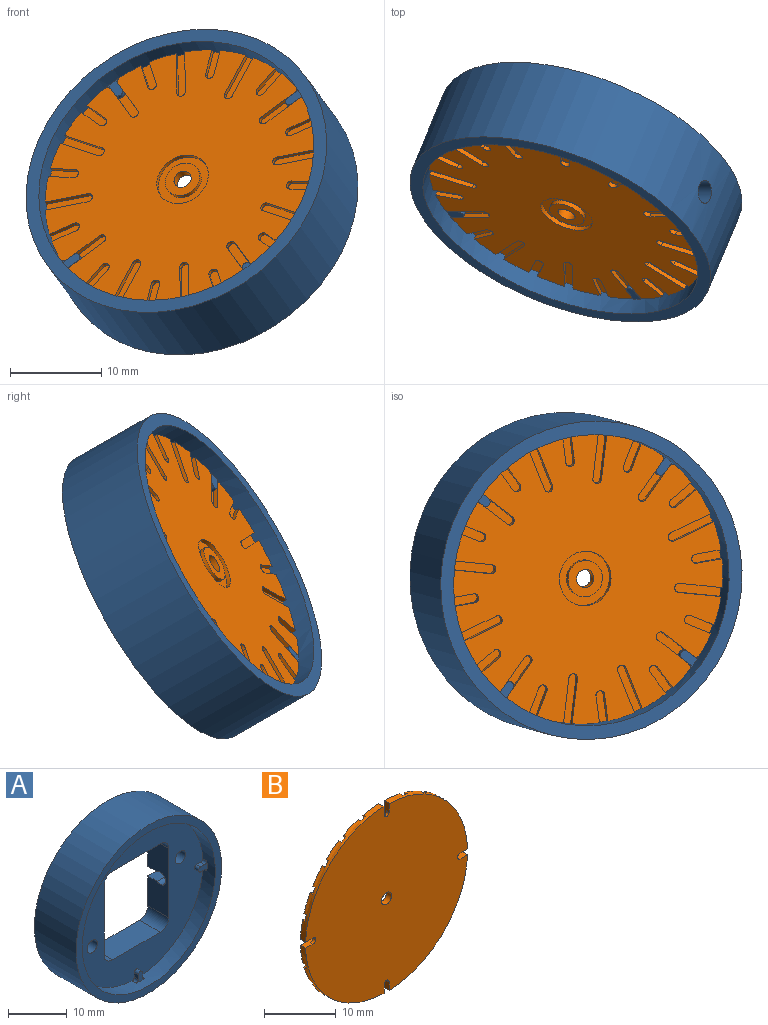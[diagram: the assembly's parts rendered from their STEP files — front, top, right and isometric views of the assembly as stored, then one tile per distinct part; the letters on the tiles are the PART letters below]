
ASSEMBLY  parts=2 mates=1
PART A: 45 faces, bbox 35x10x35 mm
  f0: cylinder r=16mm len=32mm, axis (0,-1,0), area 293.3mm2, adj f1,f7,f21,f25,f29,f33,f37,f38
  f1: plane 31.94x31.94mm, normal (0,-1,0), area 504.1mm2, adj f0,f2,f3,f4,f5,f11,f12,f13
  f2: plane 14.41x5mm, normal (-1,0,0), area 63.3mm2, adj f1,f10,f13,f14,f17,f19,f20
  f3: plane 11.52x5mm, normal (0,0,1), area 57.6mm2, adj f1,f10,f12,f14
  f4: plane 14.41x5mm, normal (1,0,0), area 72mm2, adj f1,f10,f11,f12
  f5: plane 11.52x5mm, normal (0,0,-1), area 57.6mm2, adj f1,f10,f11,f13
  f6: plane 35x35mm, normal (0,1,0), area 346.4mm2, adj f8,f9
  f7: plane 35x35mm, normal (0,-1,0), area 157.9mm2, adj f0,f8
  f8: cylinder r=17.5mm len=35mm, axis (0,-1,0), area 1094.7mm2, adj f6,f7,f17
  f9: cylinder r=14mm len=28mm, axis (0,1,0), area 175.9mm2, adj f6,f10
  f10: plane 28x28mm, normal (0,1,0), area 311.6mm2, adj f2,f3,f4,f5,f9,f11,f12,f13
  f11: cylinder r=2mm len=5mm, axis (0,1,0), area 15.7mm2, adj f1,f4,f5,f10
  f12: cylinder r=2mm len=5mm, axis (0,1,0), area 15.7mm2, adj f1,f3,f4,f10
  f13: cylinder r=2mm len=5mm, axis (0,1,0), area 15.7mm2, adj f1,f2,f5,f10
  f14: cylinder r=2mm len=5mm, axis (0,1,0), area 15.7mm2, adj f1,f2,f3,f10
  f15: cylinder r=1.25mm len=5mm, axis (0,1,0), area 39.3mm2, adj f1,f10
  f16: cylinder r=1.25mm len=5mm, axis (0,1,0), area 39.3mm2, adj f1,f10
  f17: cylinder r=1.25mm len=9.74mm, axis (-1,0,0), area 62.4mm2, adj f2,f8,f18,f19,f20
  f18: cylinder r=1mm len=2.25mm, axis (0,1,0), area 6.2mm2, adj f10,f17,f19,f20
  f19: plane 5.24x2.25mm, normal (0,0,-1), area 11.8mm2, adj f2,f10,f17,f18
  f20: plane 5.24x2.25mm, normal (0,0,1), area 11.8mm2, adj f2,f10,f17,f18
  f21: plane 2.06x2mm, normal (0,-1,0), area 2mm2, adj f0,f22,f23,f24,f43,f44
  f22: plane 1x0.97mm, normal (-1,0,0), area 1mm2, adj f1,f21,f24,f43
  f23: plane 1x0.97mm, normal (1,0,0), area 1mm2, adj f1,f21,f24,f44
  f24: cylinder r=0.5mm len=1mm, axis (0,1,0), area 1.6mm2, adj f1,f21,f22,f23
  f25: plane 2.06x2mm, normal (0,-1,0), area 2mm2, adj f0,f26,f27,f28,f39,f40
  f26: plane 1x0.97mm, normal (0,0,1), area 1mm2, adj f1,f25,f28,f39
  f27: plane 1x0.97mm, normal (0,0,-1), area 1mm2, adj f1,f25,f28,f40
  f28: cylinder r=0.5mm len=1mm, axis (0,1,0), area 1.6mm2, adj f1,f25,f26,f27
  f29: plane 2.06x2mm, normal (0,-1,0), area 2mm2, adj f0,f30,f31,f32,f37,f38
  f30: plane 1x0.97mm, normal (1,0,0), area 1mm2, adj f1,f29,f32,f37
  f31: plane 1x0.97mm, normal (-1,0,0), area 1mm2, adj f1,f29,f32,f38
  f32: cylinder r=0.5mm len=1mm, axis (0,1,0), area 1.6mm2, adj f1,f29,f30,f31
  f33: plane 2.06x2mm, normal (0,-1,0), area 2mm2, adj f0,f34,f35,f36,f41,f42
  f34: plane 1x0.97mm, normal (0,0,-1), area 1mm2, adj f1,f33,f36,f41
  f35: plane 1x0.97mm, normal (0,0,1), area 1mm2, adj f1,f33,f36,f42
  f36: cylinder r=0.5mm len=1mm, axis (0,1,0), area 1.6mm2, adj f1,f33,f34,f35
  f37: cylinder r=0.5mm len=1mm, axis (0,-1,0), area 0.8mm2, adj f0,f1,f29,f30
  f38: cylinder r=0.5mm len=1mm, axis (0,-1,0), area 0.8mm2, adj f0,f1,f29,f31
  f39: cylinder r=0.5mm len=1mm, axis (0,-1,0), area 0.8mm2, adj f0,f1,f25,f26
  f40: cylinder r=0.5mm len=1mm, axis (0,-1,0), area 0.8mm2, adj f0,f1,f25,f27
  f41: cylinder r=0.5mm len=1mm, axis (0,-1,0), area 0.8mm2, adj f0,f1,f33,f34
  f42: cylinder r=0.5mm len=1mm, axis (0,-1,0), area 0.8mm2, adj f0,f1,f33,f35
  f43: cylinder r=0.5mm len=1mm, axis (0,-1,0), area 0.8mm2, adj f0,f1,f21,f22
  f44: cylinder r=0.5mm len=1mm, axis (0,-1,0), area 0.8mm2, adj f0,f1,f21,f23
PART B: 115 faces, bbox 32x1x32 mm
  f0: plane 4x4mm, normal (0,1,0), area 9.4mm2, adj f103,f114
  f1: cylinder r=16mm len=15.49mm, axis (0,-1,0), area 21.6mm2, adj f5,f6,f10,f11,f12,f13,f15,f16
  f2: cylinder r=16mm len=15.49mm, axis (0,-1,0), area 21.6mm2, adj f5,f6,f8,f61,f63,f64,f66,f67
  f3: cylinder r=16mm len=15.49mm, axis (0,-1,0), area 21.6mm2, adj f5,f6,f37,f60,f71,f72,f73,f75
  f4: cylinder r=16mm len=15.49mm, axis (0,-1,0), area 21.6mm2, adj f5,f6,f30,f36,f39,f40,f41,f43
  f5: plane 31.98x31.98mm, normal (0,1,0), area 670.6mm2, adj f1,f2,f3,f4,f8,f9,f10,f12
  f6: plane 31.98x31.98mm, normal (0,-1,0), area 793.5mm2, adj f1,f2,f3,f4,f8,f10,f28,f30
  f7: plane 4x1mm, normal (0,1,0), area 3.5mm2, adj f8,f9,f10,f106,f107
  f8: plane 4.99x1mm, normal (-1,0,0), area 3.2mm2, adj f2,f5,f6,f7,f9,f106
  f9: cylinder r=0.5mm len=1mm, axis (0,1,0), area 0.8mm2, adj f5,f7,f8,f10
  f10: plane 4.99x1mm, normal (1,0,0), area 3.2mm2, adj f1,f5,f6,f7,f9,f107
  f11: plane 2.97x2.97mm, normal (0,1,0), area 3.4mm2, adj f1,f12,f13,f14
  f12: plane 2.12x2.12mm, normal (0.71,0,-0.71), area 1.5mm2, adj f1,f5,f11,f14
  f13: plane 2.12x2.12mm, normal (-0.71,0,0.71), area 1.5mm2, adj f1,f5,f11,f14
  f14: cylinder r=0.5mm len=0.85mm, axis (0,1,0), area 0.8mm2, adj f5,f11,f12,f13
  f15: plane 5.07x3.43mm, normal (0,1,0), area 5.4mm2, adj f1,f16,f17,f18
  f16: plane 4.32x2.5mm, normal (-0.5,0,0.87), area 2.5mm2, adj f1,f5,f15,f17
  f17: cylinder r=0.5mm len=0.93mm, axis (0,1,0), area 0.8mm2, adj f5,f15,f16,f18
  f18: plane 4.32x2.5mm, normal (0.5,0,-0.87), area 2.5mm2, adj f1,f5,f15,f17
  f19: plane 5.07x3.43mm, normal (0,1,0), area 5.4mm2, adj f1,f20,f21,f22
  f20: plane 4.32x2.5mm, normal (-0.87,0,0.5), area 2.5mm2, adj f1,f5,f19,f21
  f21: cylinder r=0.5mm len=0.93mm, axis (0,1,0), area 0.8mm2, adj f5,f19,f20,f22
  f22: plane 4.32x2.5mm, normal (0.87,0,-0.5), area 2.5mm2, adj f1,f5,f19,f21
  f23: plane 3.52x1.76mm, normal (0,1,0), area 3.4mm2, adj f1,f24,f25,f26
  f24: plane 2.89x0.77mm, normal (-0.97,0,0.26), area 1.5mm2, adj f1,f5,f23,f26
  f25: plane 2.89x0.77mm, normal (0.97,0,-0.26), area 1.5mm2, adj f1,f5,f23,f26
  f26: cylinder r=0.5mm len=0.98mm, axis (0,1,0), area 0.8mm2, adj f5,f23,f24,f25
  f27: plane 4x1mm, normal (0,1,0), area 3.5mm2, adj f28,f29,f30,f108,f109
  f28: plane 4.99x1mm, normal (0,0,1), area 3.2mm2, adj f1,f5,f6,f27,f29,f108
  f29: cylinder r=0.5mm len=1mm, axis (0,1,0), area 0.8mm2, adj f5,f27,f28,f30
  f30: plane 4.99x1mm, normal (0,0,-1), area 3.2mm2, adj f4,f5,f6,f27,f29,f109
  f31: plane 3.52x1.76mm, normal (0,1,0), area 3.4mm2, adj f1,f32,f33,f34
  f32: plane 2.89x0.77mm, normal (0.26,0,-0.97), area 1.5mm2, adj f1,f5,f31,f34
  f33: plane 2.89x0.77mm, normal (-0.26,0,0.97), area 1.5mm2, adj f1,f5,f31,f34
  f34: cylinder r=0.5mm len=0.98mm, axis (0,1,0), area 0.8mm2, adj f5,f31,f32,f33
  f35: plane 4x1mm, normal (0,1,0), area 3.5mm2, adj f36,f37,f38,f110,f111
  f36: plane 4.99x1mm, normal (1,0,0), area 3.2mm2, adj f4,f5,f6,f35,f38,f110
  f37: plane 4.99x1mm, normal (-1,0,0), area 3.2mm2, adj f3,f5,f6,f35,f38,f111
  f38: cylinder r=0.5mm len=1mm, axis (0,1,0), area 0.8mm2, adj f5,f35,f36,f37
  f39: plane 3.52x1.76mm, normal (0,1,0), area 3.4mm2, adj f4,f40,f41,f42
  f40: plane 2.89x0.77mm, normal (-0.97,0,-0.26), area 1.5mm2, adj f4,f5,f39,f42
  f41: plane 2.89x0.77mm, normal (0.97,0,0.26), area 1.5mm2, adj f4,f5,f39,f42
  f42: cylinder r=0.5mm len=0.98mm, axis (0,1,0), area 0.8mm2, adj f5,f39,f40,f41
  f43: plane 5.07x3.43mm, normal (0,1,0), area 5.4mm2, adj f4,f44,f45,f46
  f44: plane 4.32x2.5mm, normal (0.87,0,0.5), area 2.5mm2, adj f4,f5,f43,f46
  f45: plane 4.32x2.5mm, normal (-0.87,0,-0.5), area 2.5mm2, adj f4,f5,f43,f46
  f46: cylinder r=0.5mm len=0.93mm, axis (0,1,0), area 0.8mm2, adj f5,f43,f44,f45
  f47: plane 3.52x1.76mm, normal (0,1,0), area 3.4mm2, adj f4,f48,f49,f50
  f48: plane 2.89x0.77mm, normal (-0.26,0,-0.97), area 1.5mm2, adj f4,f5,f47,f50
  f49: plane 2.89x0.77mm, normal (0.26,0,0.97), area 1.5mm2, adj f4,f5,f47,f50
  f50: cylinder r=0.5mm len=0.98mm, axis (0,1,0), area 0.8mm2, adj f5,f47,f48,f49
  f51: plane 5.07x3.43mm, normal (0,1,0), area 5.4mm2, adj f4,f52,f53,f54
  f52: plane 4.32x2.5mm, normal (0.5,0,0.87), area 2.5mm2, adj f4,f5,f51,f54
  f53: plane 4.32x2.5mm, normal (-0.5,0,-0.87), area 2.5mm2, adj f4,f5,f51,f54
  f54: cylinder r=0.5mm len=0.93mm, axis (0,1,0), area 0.8mm2, adj f5,f51,f52,f53
  f55: plane 2.97x2.97mm, normal (0,1,0), area 3.4mm2, adj f4,f56,f57,f58
  f56: plane 2.12x2.12mm, normal (-0.71,0,-0.71), area 1.5mm2, adj f4,f5,f55,f58
  f57: plane 2.12x2.12mm, normal (0.71,0,0.71), area 1.5mm2, adj f4,f5,f55,f58
  f58: cylinder r=0.5mm len=0.85mm, axis (0,1,0), area 0.8mm2, adj f5,f55,f56,f57
  f59: plane 4x1mm, normal (0,1,0), area 3.5mm2, adj f60,f61,f62,f104,f105
  f60: plane 4.99x1mm, normal (0,0,-1), area 3.2mm2, adj f3,f5,f6,f59,f62,f105
  f61: plane 4.99x1mm, normal (0,0,1), area 3.2mm2, adj f2,f5,f6,f59,f62,f104
  f62: cylinder r=0.5mm len=1mm, axis (0,1,0), area 0.8mm2, adj f5,f59,f60,f61
  f63: plane 5.07x3.43mm, normal (0,1,0), area 5.4mm2, adj f2,f64,f65,f66
  f64: plane 4.32x2.5mm, normal (-0.5,0,-0.87), area 2.5mm2, adj f2,f5,f63,f65
  f65: cylinder r=0.5mm len=0.93mm, axis (0,1,0), area 0.8mm2, adj f5,f63,f64,f66
  f66: plane 4.32x2.5mm, normal (0.5,0,0.87), area 2.5mm2, adj f2,f5,f63,f65
  f67: plane 2.97x2.97mm, normal (0,1,0), area 3.4mm2, adj f2,f68,f69,f70
  f68: plane 2.12x2.12mm, normal (0.71,0,0.71), area 1.5mm2, adj f2,f5,f67,f70
  f69: plane 2.12x2.12mm, normal (-0.71,0,-0.71), area 1.5mm2, adj f2,f5,f67,f70
  f70: cylinder r=0.5mm len=0.85mm, axis (0,1,0), area 0.8mm2, adj f5,f67,f68,f69
  f71: plane 2.97x2.97mm, normal (0,1,0), area 3.4mm2, adj f3,f72,f73,f74
  f72: plane 2.12x2.12mm, normal (-0.71,0,0.71), area 1.5mm2, adj f3,f5,f71,f74
  f73: plane 2.12x2.12mm, normal (0.71,0,-0.71), area 1.5mm2, adj f3,f5,f71,f74
  f74: cylinder r=0.5mm len=0.85mm, axis (0,1,0), area 0.8mm2, adj f5,f71,f72,f73
  f75: plane 5.07x3.43mm, normal (0,1,0), area 5.4mm2, adj f3,f76,f77,f78
  f76: plane 4.32x2.5mm, normal (0.87,0,-0.5), area 2.5mm2, adj f3,f5,f75,f78
  f77: plane 4.32x2.5mm, normal (-0.87,0,0.5), area 2.5mm2, adj f3,f5,f75,f78
  f78: cylinder r=0.5mm len=0.93mm, axis (0,1,0), area 0.8mm2, adj f5,f75,f76,f77
  f79: plane 3.52x1.76mm, normal (0,1,0), area 3.4mm2, adj f3,f80,f81,f82
  f80: plane 2.89x0.77mm, normal (-0.97,0,0.26), area 1.5mm2, adj f3,f5,f79,f82
  f81: plane 2.89x0.77mm, normal (0.97,0,-0.26), area 1.5mm2, adj f3,f5,f79,f82
  f82: cylinder r=0.5mm len=0.98mm, axis (0,1,0), area 0.8mm2, adj f5,f79,f80,f81
  f83: plane 3.52x1.76mm, normal (0,1,0), area 3.4mm2, adj f3,f84,f85,f86
  f84: plane 2.89x0.77mm, normal (-0.26,0,0.97), area 1.5mm2, adj f3,f5,f83,f86
  f85: plane 2.89x0.77mm, normal (0.26,0,-0.97), area 1.5mm2, adj f3,f5,f83,f86
  f86: cylinder r=0.5mm len=0.98mm, axis (0,1,0), area 0.8mm2, adj f5,f83,f84,f85
  f87: plane 3.52x1.76mm, normal (0,1,0), area 3.4mm2, adj f2,f88,f89,f90
  f88: plane 2.89x0.77mm, normal (0.26,0,0.97), area 1.5mm2, adj f2,f5,f87,f90
  f89: plane 2.89x0.77mm, normal (-0.26,0,-0.97), area 1.5mm2, adj f2,f5,f87,f90
  f90: cylinder r=0.5mm len=0.98mm, axis (0,1,0), area 0.8mm2, adj f5,f87,f88,f89
  f91: plane 5.07x3.43mm, normal (0,1,0), area 5.4mm2, adj f3,f92,f93,f94
  f92: plane 4.32x2.5mm, normal (0.5,0,-0.87), area 2.5mm2, adj f3,f5,f91,f94
  f93: plane 4.32x2.5mm, normal (-0.5,0,0.87), area 2.5mm2, adj f3,f5,f91,f94
  f94: cylinder r=0.5mm len=0.93mm, axis (0,1,0), area 0.8mm2, adj f5,f91,f92,f93
  f95: plane 5.07x3.43mm, normal (0,1,0), area 5.4mm2, adj f2,f96,f97,f98
  f96: plane 4.32x2.5mm, normal (-0.87,0,-0.5), area 2.5mm2, adj f2,f5,f95,f98
  f97: plane 4.32x2.5mm, normal (0.87,0,0.5), area 2.5mm2, adj f2,f5,f95,f98
  f98: cylinder r=0.5mm len=0.93mm, axis (0,1,0), area 0.8mm2, adj f5,f95,f96,f97
  f99: plane 2.89x0.77mm, normal (0.97,0,0.26), area 1.5mm2, adj f2,f5,f101,f102
  f100: plane 2.89x0.77mm, normal (-0.97,0,-0.26), area 1.5mm2, adj f2,f5,f101,f102
  f101: cylinder r=0.5mm len=0.98mm, axis (0,1,0), area 0.8mm2, adj f5,f99,f100,f102
  f102: plane 3.52x1.76mm, normal (0,1,0), area 3.4mm2, adj f2,f99,f100,f101
  f103: cylinder r=1mm len=2mm, axis (0,1,0), area 6.3mm2, adj f0,f6
  f104: cylinder r=0.5mm len=0.5mm, axis (0,-1,0), area 0.4mm2, adj f6,f59,f61,f105
  f105: cylinder r=0.5mm len=0.5mm, axis (0,1,0), area 0.4mm2, adj f6,f59,f60,f104
  f106: cylinder r=0.5mm len=0.5mm, axis (0,1,0), area 0.4mm2, adj f6,f7,f8,f107
  f107: cylinder r=0.5mm len=0.5mm, axis (0,-1,0), area 0.4mm2, adj f6,f7,f10,f106
  f108: cylinder r=0.5mm len=0.5mm, axis (0,1,0), area 0.4mm2, adj f6,f27,f28,f109
  f109: cylinder r=0.5mm len=0.5mm, axis (0,-1,0), area 0.4mm2, adj f6,f27,f30,f108
  f110: cylinder r=0.5mm len=0.5mm, axis (0,1,0), area 0.4mm2, adj f6,f35,f36,f111
  f111: cylinder r=0.5mm len=0.5mm, axis (0,-1,0), area 0.4mm2, adj f6,f35,f37,f110
  f112: cylinder r=3mm len=6mm, axis (0,1,0), area 9.4mm2, adj f5,f113
  f113: plane 6x6mm, normal (0,1,0), area 15.7mm2, adj f112,f114
  f114: cylinder r=2mm len=4mm, axis (0,1,0), area 6.3mm2, adj f0,f113
PLACE A rot(axis=(-0.68,-0.7,-0.22),50.1deg) t=(-11.95,-0.33,-30.93)mm
PLACE B rot(axis=(0.95,-0.1,0.31),146.6deg) t=(-10.93,2.12,-32.33)mm
MATE fastened A.f8 <-> B.f1  axis (-0.34,-0.82,0.47) through (-10.93,2.12,-32.33)mm
